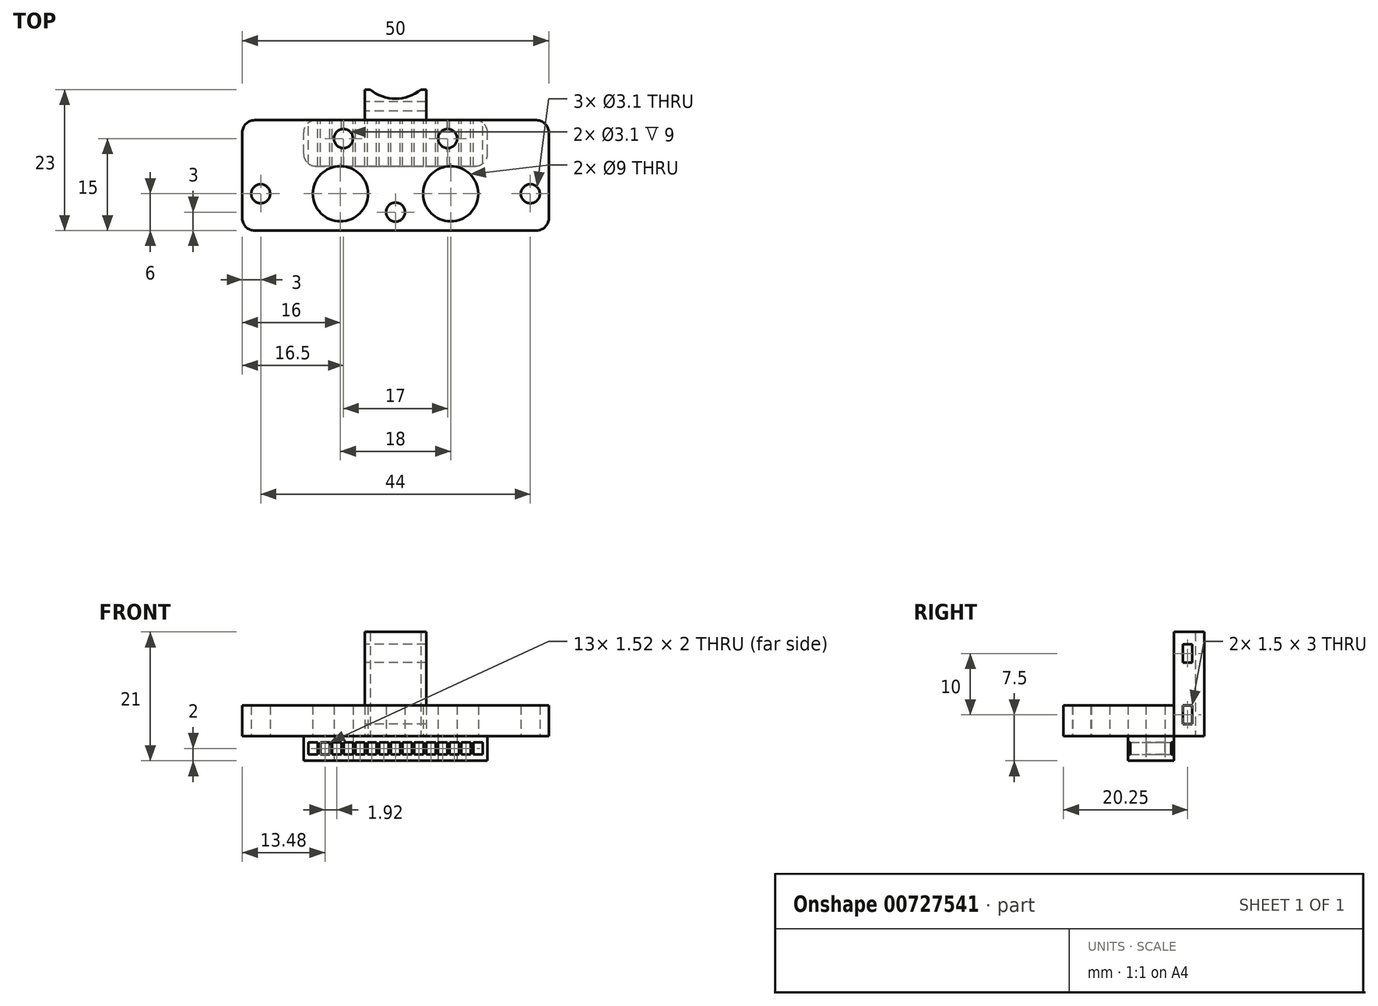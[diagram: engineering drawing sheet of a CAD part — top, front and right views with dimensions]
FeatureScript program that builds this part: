
annotation { "Feature Type Name" : "Feature", "Feature Type Description" : "" }
export const myFeature = defineFeature(function(context is Context, id is Id, definition is map)
    precondition{}
    {
        {
            var Q0;
            Q0=qCreatedBy(makeId("Top.planeOp"),FACE);
            var sketch = newSketch(context, id + "F0", { "sketchPlane" : qUnion([Q0]), "disableImprinting" : false});
            skLineSegment(sketch, "E0.bottom", {"start": v(0, 0) * mm, "end": v(30, 0) * mm});
            skLineSegment(sketch, "E0.top", {"start": v(0, 18) * mm, "end": v(30, 18) * mm});
            skLineSegment(sketch, "E0.left", {"start": v(0, 0) * mm, "end": v(0, 18) * mm});
            skLineSegment(sketch, "E0.right", {"start": v(30, 0) * mm, "end": v(30, 18) * mm});
            skCircle(sketch, "E1", {"center": v(6.5, 15) * mm, "radius": 1.55 * mm});
            skCircle(sketch, "E2", {"center": v(15, 3) * mm, "radius": 1.55 * mm});
            skCircle(sketch, "E3", {"center": v(23.5, 15) * mm, "radius": 1.55 * mm});
            skCircle(sketch, "E4", {"center": v(6, 6) * mm, "radius": 4.5 * mm});
            skCircle(sketch, "E5", {"center": v(24, 6) * mm, "radius": 4.5 * mm});
            skLineSegment(sketch, "E6.bottom", {"start": v(0, 18) * mm, "end": v(-10, 18) * mm});
            skLineSegment(sketch, "E6.top", {"start": v(0, 0) * mm, "end": v(-10, 0) * mm});
            skLineSegment(sketch, "E6.left", {"start": v(0, 18) * mm, "end": v(0, 0) * mm});
            skLineSegment(sketch, "E6.right", {"start": v(-10, 18) * mm, "end": v(-10, 0) * mm});
            skLineSegment(sketch, "E7.bottom", {"start": v(30, 18) * mm, "end": v(40, 18) * mm});
            skLineSegment(sketch, "E7.top", {"start": v(30, 0) * mm, "end": v(40, 0) * mm});
            skLineSegment(sketch, "E7.left", {"start": v(30, 18) * mm, "end": v(30, 0) * mm});
            skLineSegment(sketch, "E7.right", {"start": v(40, 18) * mm, "end": v(40, 0) * mm});
            skCircle(sketch, "E8", {"center": v(-7, 6) * mm, "radius": 1.55 * mm});
            skCircle(sketch, "E9", {"center": v(37, 6) * mm, "radius": 1.55 * mm});
            skLineSegment(sketch, "E10", {"start": v(10.5, 0) * mm, "end": v(10.5, 6) * mm});
            skLineSegment(sketch, "E11", {"start": v(19.5, 0) * mm, "end": v(19.5, 6) * mm});
            skLineSegment(sketch, "E12", {"start": v(0, 10.5) * mm, "end": v(30, 10.5) * mm});
            skLineSegment(sketch, "E13.bottom", {"start": v(30, 18) * mm, "end": v(0, 18) * mm});
            skCircle(sketch, "E14", {"center": v(15, 28) * mm, "radius": 6.5 * mm});
            skLineSegment(sketch, "E15.bottom", {"start": v(20, 18) * mm, "end": v(10, 18) * mm});
            skLineSegment(sketch, "E15.top", {"start": v(20, 23) * mm, "end": v(10, 23) * mm});
            skLineSegment(sketch, "E15.left", {"start": v(20, 18) * mm, "end": v(20, 23) * mm});
            skLineSegment(sketch, "E15.right", {"start": v(10, 18) * mm, "end": v(10, 23) * mm});
            skSolve(sketch);
        }
        {
            var Q0;
            Q0=makeQuery(id+"F0.imprint","IMPRINT",FACE,{"disambiguationData":[TD([[makeQuery(id+"F0.imprint","IMPRINT",EDGE,{"derivedFrom":sQuery(id+"F0.wireOp",EDGE,"E0.left")}),1.0]])]});
            var Q1;
            Q1=makeQuery(id+"F0.imprint","IMPRINT",FACE,{"disambiguationData":[TD([[makeQuery(id+"F0.imprint","IMPRINT",EDGE,{"derivedFrom":sQuery(id+"F0.wireOp",EDGE,"E0.bottom")}),1.0]])]});
            var Q2;
            Q2=makeQuery(id+"F0.imprint","IMPRINT",FACE,{"disambiguationData":[TD([[makeQuery(id+"F0.imprint","IMPRINT",EDGE,{"derivedFrom":sQuery(id+"F0.wireOp",EDGE,"E0.right")}),-1.0]])]});
            var Q3;
            {var subQ0=sQuery(id+"F0.wireOp",EDGE,"vLEq8gqX-rGJx-hqH1-taDU-eSVpu49ErQbJ");Q3=makeQuery(id+"F0.imprint","IMPRINT",FACE,{"disambiguationData":[TD([[makeQuery(id+"F0.imprint","IMPRINT",EDGE,{"derivedFrom":subQ0}),-1.0]])]});}
            var Q4;
            {var subQ0=sQuery(id+"F0.wireOp",EDGE,"E11");Q4=makeQuery(id+"F0.imprint","IMPRINT",FACE,{"disambiguationData":[TD([[makeQuery(id+"F0.imprint","IMPRINT",EDGE,{"derivedFrom":subQ0}),-1.0]])]});}
            var Q5;
            {var subQ1=sQuery(id+"F0.wireOp",EDGE,"E0.top");Q5=makeQuery(id+"F0.imprint","IMPRINT",FACE,{"disambiguationData":[TD([[makeQuery(id+"F0.imprint","IMPRINT",EDGE,{"derivedFrom":subQ1}),-1.0]])]});}
            var Q6;
            Q6=makeQuery(id+"F0.imprint","IMPRINT",FACE,{"disambiguationData":[TD([[makeQuery(id+"F0.imprint","IMPRINT",EDGE,{"derivedFrom":sQuery(id+"F0.wireOp",EDGE,"E2")}),-1.0]])]});
            extrude(context, id + "F1", {"entities" : qUnion([Q0, Q1, Q2, Q3, Q4, Q5, Q6]), "depth" : 5 * mm, "offsetDistance" : 25 * mm});
        }
        {
            var Q0;
            {var subQ1=sQuery(id+"F0.wireOp",EDGE,"E0.top");Q0=makeQuery(id+"F0.imprint","IMPRINT",FACE,{"disambiguationData":[TD([[makeQuery(id+"F0.imprint","IMPRINT",EDGE,{"derivedFrom":subQ1}),-1.0]])]});}
            extrude(context, id + "F2", {"entities" : qUnion([Q0]), "oppositeDirection" : true, "depth" : 4 * mm, "offsetDistance" : 25 * mm});
        }
        {
            var Q0;
            {var subQ5=sQuery(id+"F0.wireOp",EDGE,"E15.left");Q0=makeQuery(id+"F0.imprint","IMPRINT",FACE,{"disambiguationData":[TD([[makeQuery(id+"F0.imprint","IMPRINT",EDGE,{"derivedFrom":subQ5}),1.0]])]});}
            extrude(context, id + "F3", {"entities" : qUnion([Q0]), "operationType" : NewBodyOperationType.ADD, "depth" : 17 * mm, "offsetDistance" : 25 * mm});
        }
        {
            var Q0;
            Q0=makeQuery(id+"F3.opExtrude","SWEPT_FACE",FACE,{"disambiguationData":[OSD([sQuery(id+"F0.wireOp",EDGE,"E15.right")])]});
            var sketch = newSketch(context, id + "F4", { "sketchPlane" : qUnion([Q0])});
            skLineSegment(sketch, "E16.bottom", {"start": v(-21, 5) * mm, "end": v(-19.5, 5) * mm});
            skLineSegment(sketch, "E16.top", {"start": v(-21, 2) * mm, "end": v(-19.5, 2) * mm});
            skLineSegment(sketch, "E16.left", {"start": v(-21, 5) * mm, "end": v(-21, 2) * mm});
            skLineSegment(sketch, "E16.right", {"start": v(-19.5, 5) * mm, "end": v(-19.5, 2) * mm});
            skLineSegment(sketch, "E17.bottom", {"start": v(-21, 15) * mm, "end": v(-19.5, 15) * mm});
            skLineSegment(sketch, "E17.top", {"start": v(-21, 12) * mm, "end": v(-19.5, 12) * mm});
            skLineSegment(sketch, "E17.left", {"start": v(-21, 15) * mm, "end": v(-21, 12) * mm});
            skLineSegment(sketch, "E17.right", {"start": v(-19.5, 15) * mm, "end": v(-19.5, 12) * mm});
            skSolve(sketch);
        }
        {
            var Q0;
            Q0=makeQuery(id+"F4.imprint","IMPRINT",FACE,{"disambiguationData":[TD([[makeQuery(id+"F4.imprint","IMPRINT",EDGE,{"derivedFrom":sQuery(id+"F4.wireOp",EDGE,"E16.bottom")}),-1.0]])]});
            var Q1;
            Q1=makeQuery(id+"F4.imprint","IMPRINT",FACE,{"disambiguationData":[TD([[makeQuery(id+"F4.imprint","IMPRINT",EDGE,{"derivedFrom":sQuery(id+"F4.wireOp",EDGE,"E17.bottom")}),-1.0]])]});
            extrude(context, id + "F5", {"entities" : qUnion([Q0, Q1]), "operationType" : NewBodyOperationType.REMOVE, "oppositeDirection" : true, "depth" : 25 * mm, "offsetDistance" : 25 * mm});
        }
        {
            var Q0;
            Q0=makeQuery(id+"F2.opExtrude","SWEPT_FACE",FACE,{"disambiguationData":[OSD([sQuery(id+"F0.wireOp",EDGE,"E0.top")])]});
            var sketch = newSketch(context, id + "F6", { "sketchPlane" : qUnion([Q0])});
            skLineSegment(sketch, "E18.bottom", {"start": v(-27.68, -3) * mm, "end": v(-29.2, -3) * mm});
            skLineSegment(sketch, "E18.top", {"start": v(-27.68, -1) * mm, "end": v(-29.2, -1) * mm});
            skLineSegment(sketch, "E18.left", {"start": v(-27.68, -3) * mm, "end": v(-27.68, -1) * mm});
            skLineSegment(sketch, "E18.right", {"start": v(-29.2, -3) * mm, "end": v(-29.2, -1) * mm});
            skLineSegment(sketch, "E19.1.0.0", {"start": v(-27.28, -3) * mm, "end": v(-27.28, -1) * mm});
            skLineSegment(sketch, "E19.1.0.1", {"start": v(-25.76, -3) * mm, "end": v(-27.28, -3) * mm});
            skLineSegment(sketch, "E19.1.0.2", {"start": v(-25.76, -1) * mm, "end": v(-27.28, -1) * mm});
            skLineSegment(sketch, "E19.1.0.3", {"start": v(-25.76, -3) * mm, "end": v(-25.76, -1) * mm});
            skLineSegment(sketch, "E19.2.0.0", {"start": v(-25.36, -3) * mm, "end": v(-25.36, -1) * mm});
            skLineSegment(sketch, "E19.2.0.1", {"start": v(-23.84, -3) * mm, "end": v(-25.36, -3) * mm});
            skLineSegment(sketch, "E19.2.0.2", {"start": v(-23.84, -1) * mm, "end": v(-25.36, -1) * mm});
            skLineSegment(sketch, "E19.2.0.3", {"start": v(-23.84, -3) * mm, "end": v(-23.84, -1) * mm});
            skLineSegment(sketch, "E19.direction1", {"start": v(-29.2, -3) * mm, "end": v(-27.28, -3) * mm, "construction": true});
            skLineSegment(sketch, "E20.0.3.0", {"start": v(-23.44, -3) * mm, "end": v(-23.44, -1) * mm});
            skLineSegment(sketch, "E20.3.3.0", {"start": v(-21.92, -3) * mm, "end": v(-23.44, -3) * mm});
            skLineSegment(sketch, "E20.6.3.0", {"start": v(-21.92, -1) * mm, "end": v(-23.44, -1) * mm});
            skLineSegment(sketch, "E20.9.3.0", {"start": v(-21.92, -3) * mm, "end": v(-21.92, -1) * mm});
            skLineSegment(sketch, "E20.0.4.0", {"start": v(-21.52, -3) * mm, "end": v(-21.52, -1) * mm});
            skLineSegment(sketch, "E20.3.4.0", {"start": v(-20, -3) * mm, "end": v(-21.52, -3) * mm});
            skLineSegment(sketch, "E20.6.4.0", {"start": v(-20, -1) * mm, "end": v(-21.52, -1) * mm});
            skLineSegment(sketch, "E20.9.4.0", {"start": v(-20, -3) * mm, "end": v(-20, -1) * mm});
            skLineSegment(sketch, "E20.0.5.0", {"start": v(-19.6, -3) * mm, "end": v(-19.6, -1) * mm});
            skLineSegment(sketch, "E20.3.5.0", {"start": v(-18.08, -3) * mm, "end": v(-19.6, -3) * mm});
            skLineSegment(sketch, "E20.6.5.0", {"start": v(-18.08, -1) * mm, "end": v(-19.6, -1) * mm});
            skLineSegment(sketch, "E20.9.5.0", {"start": v(-18.08, -3) * mm, "end": v(-18.08, -1) * mm});
            skLineSegment(sketch, "E20.0.6.0", {"start": v(-17.68, -3) * mm, "end": v(-17.68, -1) * mm});
            skLineSegment(sketch, "E20.3.6.0", {"start": v(-16.16, -3) * mm, "end": v(-17.68, -3) * mm});
            skLineSegment(sketch, "E20.6.6.0", {"start": v(-16.16, -1) * mm, "end": v(-17.68, -1) * mm});
            skLineSegment(sketch, "E20.9.6.0", {"start": v(-16.16, -3) * mm, "end": v(-16.16, -1) * mm});
            skLineSegment(sketch, "E20.0.7.0", {"start": v(-15.76, -3) * mm, "end": v(-15.76, -1) * mm});
            skLineSegment(sketch, "E20.3.7.0", {"start": v(-14.24, -3) * mm, "end": v(-15.76, -3) * mm});
            skLineSegment(sketch, "E20.6.7.0", {"start": v(-14.24, -1) * mm, "end": v(-15.76, -1) * mm});
            skLineSegment(sketch, "E20.9.7.0", {"start": v(-14.24, -3) * mm, "end": v(-14.24, -1) * mm});
            skLineSegment(sketch, "E20.0.8.0", {"start": v(-13.84, -3) * mm, "end": v(-13.84, -1) * mm});
            skLineSegment(sketch, "E20.3.8.0", {"start": v(-12.32, -3) * mm, "end": v(-13.84, -3) * mm});
            skLineSegment(sketch, "E20.6.8.0", {"start": v(-12.32, -1) * mm, "end": v(-13.84, -1) * mm});
            skLineSegment(sketch, "E20.9.8.0", {"start": v(-12.32, -3) * mm, "end": v(-12.32, -1) * mm});
            skLineSegment(sketch, "E20.0.9.0", {"start": v(-11.92, -3) * mm, "end": v(-11.92, -1) * mm});
            skLineSegment(sketch, "E20.3.9.0", {"start": v(-10.4, -3) * mm, "end": v(-11.92, -3) * mm});
            skLineSegment(sketch, "E20.6.9.0", {"start": v(-10.4, -1) * mm, "end": v(-11.92, -1) * mm});
            skLineSegment(sketch, "E20.9.9.0", {"start": v(-10.4, -3) * mm, "end": v(-10.4, -1) * mm});
            skLineSegment(sketch, "E20.0.10.0", {"start": v(-10, -3) * mm, "end": v(-10, -1) * mm});
            skLineSegment(sketch, "E20.3.10.0", {"start": v(-8.48, -3) * mm, "end": v(-10, -3) * mm});
            skLineSegment(sketch, "E20.6.10.0", {"start": v(-8.48, -1) * mm, "end": v(-10, -1) * mm});
            skLineSegment(sketch, "E20.9.10.0", {"start": v(-8.48, -3) * mm, "end": v(-8.48, -1) * mm});
            skLineSegment(sketch, "E20.0.11.0", {"start": v(-8.08, -3) * mm, "end": v(-8.08, -1) * mm});
            skLineSegment(sketch, "E20.3.11.0", {"start": v(-6.56, -3) * mm, "end": v(-8.08, -3) * mm});
            skLineSegment(sketch, "E20.6.11.0", {"start": v(-6.56, -1) * mm, "end": v(-8.08, -1) * mm});
            skLineSegment(sketch, "E20.9.11.0", {"start": v(-6.56, -3) * mm, "end": v(-6.56, -1) * mm});
            skLineSegment(sketch, "E21.0.12.0", {"start": v(-6.16, -3) * mm, "end": v(-6.16, -1) * mm});
            skLineSegment(sketch, "E21.3.12.0", {"start": v(-4.64, -3) * mm, "end": v(-6.16, -3) * mm});
            skLineSegment(sketch, "E21.6.12.0", {"start": v(-4.64, -1) * mm, "end": v(-6.16, -1) * mm});
            skLineSegment(sketch, "E21.9.12.0", {"start": v(-4.64, -3) * mm, "end": v(-4.64, -1) * mm});
            skLineSegment(sketch, "E21.0.13.0", {"start": v(-4.24, -3) * mm, "end": v(-4.24, -1) * mm});
            skLineSegment(sketch, "E21.3.13.0", {"start": v(-2.72, -3) * mm, "end": v(-4.24, -3) * mm});
            skLineSegment(sketch, "E21.6.13.0", {"start": v(-2.72, -1) * mm, "end": v(-4.24, -1) * mm});
            skLineSegment(sketch, "E21.9.13.0", {"start": v(-2.72, -3) * mm, "end": v(-2.72, -1) * mm});
            skLineSegment(sketch, "E22.0.14.0", {"start": v(-2.32, -3) * mm, "end": v(-2.32, -1) * mm});
            skLineSegment(sketch, "E22.3.14.0", {"start": v(-0.8, -3) * mm, "end": v(-2.32, -3) * mm});
            skLineSegment(sketch, "E22.6.14.0", {"start": v(-0.8, -1) * mm, "end": v(-2.32, -1) * mm});
            skLineSegment(sketch, "E22.9.14.0", {"start": v(-0.8, -3) * mm, "end": v(-0.8, -1) * mm});
            skSolve(sketch);
        }
        {
            var Q0;
            Q0=makeQuery(id+"F6.imprint","IMPRINT",FACE,{"disambiguationData":[TD([[makeQuery(id+"F6.imprint","IMPRINT",EDGE,{"derivedFrom":sQuery(id+"F6.wireOp",EDGE,"E21.0.14.0")}),-1.0]])]});
            var Q1;
            Q1=makeQuery(id+"F6.imprint","IMPRINT",FACE,{"disambiguationData":[TD([[makeQuery(id+"F6.imprint","IMPRINT",EDGE,{"derivedFrom":sQuery(id+"F6.wireOp",EDGE,"E21.0.13.0")}),-1.0]])]});
            var Q2;
            Q2=makeQuery(id+"F6.imprint","IMPRINT",FACE,{"disambiguationData":[TD([[makeQuery(id+"F6.imprint","IMPRINT",EDGE,{"derivedFrom":sQuery(id+"F6.wireOp",EDGE,"E21.0.12.0")}),-1.0]])]});
            var Q3;
            Q3=makeQuery(id+"F6.imprint","IMPRINT",FACE,{"disambiguationData":[TD([[makeQuery(id+"F6.imprint","IMPRINT",EDGE,{"derivedFrom":sQuery(id+"F6.wireOp",EDGE,"E20.0.11.0")}),-1.0]])]});
            var Q4;
            Q4=makeQuery(id+"F6.imprint","IMPRINT",FACE,{"disambiguationData":[TD([[makeQuery(id+"F6.imprint","IMPRINT",EDGE,{"derivedFrom":sQuery(id+"F6.wireOp",EDGE,"E20.0.10.0")}),-1.0]])]});
            var Q5;
            Q5=makeQuery(id+"F6.imprint","IMPRINT",FACE,{"disambiguationData":[TD([[makeQuery(id+"F6.imprint","IMPRINT",EDGE,{"derivedFrom":sQuery(id+"F6.wireOp",EDGE,"E20.0.9.0")}),-1.0]])]});
            var Q6;
            Q6=makeQuery(id+"F6.imprint","IMPRINT",FACE,{"disambiguationData":[TD([[makeQuery(id+"F6.imprint","IMPRINT",EDGE,{"derivedFrom":sQuery(id+"F6.wireOp",EDGE,"E20.0.8.0")}),-1.0]])]});
            var Q7;
            Q7=makeQuery(id+"F6.imprint","IMPRINT",FACE,{"disambiguationData":[TD([[makeQuery(id+"F6.imprint","IMPRINT",EDGE,{"derivedFrom":sQuery(id+"F6.wireOp",EDGE,"E20.0.7.0")}),-1.0]])]});
            var Q8;
            Q8=makeQuery(id+"F6.imprint","IMPRINT",FACE,{"disambiguationData":[TD([[makeQuery(id+"F6.imprint","IMPRINT",EDGE,{"derivedFrom":sQuery(id+"F6.wireOp",EDGE,"E20.0.6.0")}),-1.0]])]});
            var Q9;
            Q9=makeQuery(id+"F6.imprint","IMPRINT",FACE,{"disambiguationData":[TD([[makeQuery(id+"F6.imprint","IMPRINT",EDGE,{"derivedFrom":sQuery(id+"F6.wireOp",EDGE,"E20.0.5.0")}),-1.0]])]});
            var Q10;
            Q10=makeQuery(id+"F6.imprint","IMPRINT",FACE,{"disambiguationData":[TD([[makeQuery(id+"F6.imprint","IMPRINT",EDGE,{"derivedFrom":sQuery(id+"F6.wireOp",EDGE,"E20.0.4.0")}),-1.0]])]});
            var Q11;
            Q11=makeQuery(id+"F6.imprint","IMPRINT",FACE,{"disambiguationData":[TD([[makeQuery(id+"F6.imprint","IMPRINT",EDGE,{"derivedFrom":sQuery(id+"F6.wireOp",EDGE,"E20.0.3.0")}),-1.0]])]});
            var Q12;
            Q12=makeQuery(id+"F6.imprint","IMPRINT",FACE,{"disambiguationData":[TD([[makeQuery(id+"F6.imprint","IMPRINT",EDGE,{"derivedFrom":sQuery(id+"F6.wireOp",EDGE,"E19.2.0.0")}),-1.0]])]});
            var Q13;
            Q13=makeQuery(id+"F6.imprint","IMPRINT",FACE,{"disambiguationData":[TD([[makeQuery(id+"F6.imprint","IMPRINT",EDGE,{"derivedFrom":sQuery(id+"F6.wireOp",EDGE,"E19.1.0.0")}),-1.0]])]});
            var Q14;
            Q14=makeQuery(id+"F6.imprint","IMPRINT",FACE,{"disambiguationData":[TD([[makeQuery(id+"F6.imprint","IMPRINT",EDGE,{"derivedFrom":sQuery(id+"F6.wireOp",EDGE,"E18.bottom")}),-1.0]])]});
            var Q15;
            Q15=makeQuery(id+"F6.imprint","IMPRINT",FACE,{"disambiguationData":[TD([[makeQuery(id+"F6.imprint","IMPRINT",EDGE,{"derivedFrom":sQuery(id+"F6.wireOp",EDGE,"E22.0.14.0")}),-1.0]])]});
            extrude(context, id + "F7", {"entities" : qUnion([Q0, Q1, Q2, Q3, Q4, Q5, Q6, Q7, Q8, Q9, Q10, Q11, Q12, Q13, Q14, Q15]), "operationType" : NewBodyOperationType.REMOVE, "oppositeDirection" : true, "depth" : 11 * mm, "offsetDistance" : 25 * mm});
        }
        {
            var Q0;
            Q0=makeQuery(id+"F2.opExtrude","SWEPT_EDGE",EDGE,{"disambiguationData":[OSD([sQuery(id+"F0.wireOp",EDGE,"E0.top"),sQuery(id+"F0.wireOp",EDGE,"E0.left"),sQuery(id+"F0.wireOp",EDGE,"E6.bottom")])]});
            var Q1;
            Q1=makeQuery(id+"F2.opExtrude","SWEPT_EDGE",EDGE,{"disambiguationData":[OSD([sQuery(id+"F0.wireOp",EDGE,"E0.top"),sQuery(id+"F0.wireOp",EDGE,"E0.right"),sQuery(id+"F0.wireOp",EDGE,"E7.bottom")])]});
            var Q2;
            Q2=makeQuery(id+"F2.opExtrude","SWEPT_EDGE",EDGE,{"disambiguationData":[OSD([sQuery(id+"F0.wireOp",EDGE,"E0.right"),sQuery(id+"F0.wireOp",EDGE,"E12")])]});
            var Q3;
            Q3=makeQuery(id+"F2.opExtrude","SWEPT_EDGE",EDGE,{"disambiguationData":[OSD([sQuery(id+"F0.wireOp",EDGE,"E0.bottom"),sQuery(id+"F0.wireOp",EDGE,"E11")])]});
            var Q4;
            Q4=makeQuery(id+"F2.opExtrude","SWEPT_EDGE",EDGE,{"disambiguationData":[OSD([sQuery(id+"F0.wireOp",EDGE,"E0.bottom"),sQuery(id+"F0.wireOp",EDGE,"E10")])]});
            var Q5;
            Q5=makeQuery(id+"F2.opExtrude","SWEPT_EDGE",EDGE,{"disambiguationData":[OSD([sQuery(id+"F0.wireOp",EDGE,"E0.left"),sQuery(id+"F0.wireOp",EDGE,"E12")])]});
            var Q6;
            Q6=makeQuery(id+"F1.opExtrude","SWEPT_EDGE",EDGE,{"disambiguationData":[OSD([sQuery(id+"F0.wireOp",EDGE,"E6.top"),sQuery(id+"F0.wireOp",EDGE,"E6.right")])]});
            var Q7;
            Q7=makeQuery(id+"F1.opExtrude","SWEPT_EDGE",EDGE,{"disambiguationData":[OSD([sQuery(id+"F0.wireOp",EDGE,"E7.top"),sQuery(id+"F0.wireOp",EDGE,"E7.right")])]});
            var Q8;
            Q8=makeQuery(id+"F1.opExtrude","SWEPT_EDGE",EDGE,{"disambiguationData":[OSD([sQuery(id+"F0.wireOp",EDGE,"E7.bottom"),sQuery(id+"F0.wireOp",EDGE,"E7.right")])]});
            var Q9;
            Q9=makeQuery(id+"F1.opExtrude","SWEPT_EDGE",EDGE,{"disambiguationData":[OSD([sQuery(id+"F0.wireOp",EDGE,"E6.bottom"),sQuery(id+"F0.wireOp",EDGE,"E6.right")])]});
            fillet(context, id + "F8", {"entities" : qUnion([Q0, Q1, Q2, Q3, Q4, Q5, Q6, Q7, Q8, Q9]), "tangentPropagation" : true, "radius" : 2 * mm, "defaultsChanged" : false, "vertexSettings" : [], "allowEdgeOverflow" : false});
        }
    });
